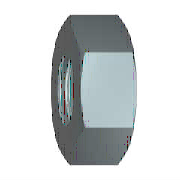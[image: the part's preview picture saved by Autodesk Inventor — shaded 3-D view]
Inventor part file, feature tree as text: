
AUTODESK INVENTOR PART (.ipt)
format: ipt  version: 2023.2 (Build 272271030, 271C)  size: 161,280 bytes
history: native  units: mm (DEFAULTED — no unit token found)
features: sketch x3, chamfer x1, hole x1, other x1, plane x1
ambient origin geometry x7: Origin, YZ Plane, XZ Plane, X Axis, Y Axis, Z Axis, Center Point
bodies: Solid1 (feature_tree), Body (feature_tree)
feature tree (7):
  chamfer  "Chamfer1"  Angle=30.0deg  [1 undecoded]
  hole  "Thread"  [1 undecoded]
  other  "Work Axis1"
  plane  "Work Plane1"
  sketch  "Sketch1"  dims[d0=18.475209mm]
  sketch  "Sketch2"  dims[d1=8.4mm]
  sketch  "Sketch3"  dims[d2=0.0mm d3=30.0deg d4=30.0deg d5=14.63mm d6=14.63mm d7=90.0deg d25=8.917468mm d26=6.0mm d27=4.0mm d28=2.0mm d29=14.3117mm d30=8.0mm d31=20.594885mm d8=0.541266mm d9=30.0deg d10=0.541266mm d11=30.0deg d13=0.0mm d14=0.0mm d39=0.0mm d40=0.541266mm d41=0.541266mm d42=0.0mm]
note: 2 required parameter values undecoded (feature->parameter linkage not recoverable at this tier; creation-order binding heuristic only, values carry confidence <= 0.55)
